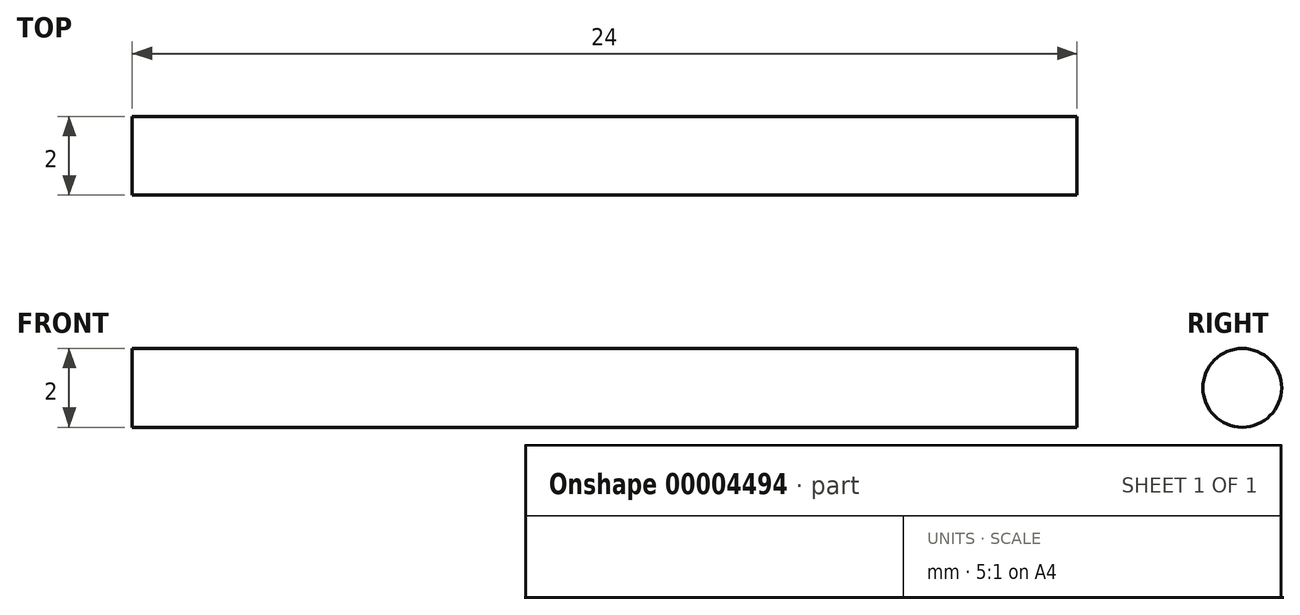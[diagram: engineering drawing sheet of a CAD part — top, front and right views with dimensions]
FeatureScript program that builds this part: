
annotation { "Feature Type Name" : "Feature", "Feature Type Description" : "" }
export const myFeature = defineFeature(function(context is Context, id is Id, definition is map)
    precondition{}
    {
        {
            var Q0;
            Q0=qCreatedBy(makeId("Right.planeOp"),FACE);
            var sketch = newSketch(context, id + "F0", { "sketchPlane" : qUnion([Q0])});
            skCircle(sketch, "E0", {"center": v(0, 0) * mm, "radius": 1 * mm});
            skSolve(sketch);
        }
        {
            var Q0;
            Q0=makeQuery(id+"F0.imprint","IMPRINT",FACE,{"disambiguationData":[TD([[makeQuery(id+"F0.imprint","IMPRINT",EDGE,{"derivedFrom":sQuery(id+"F0.wireOp",EDGE,"E0")}),1.0]])]});
            extrude(context, id + "F1", {"entities" : qUnion([Q0]), "endBound" : BoundingType.SYMMETRIC, "depth" : (20 + 4) * mm});
        }
    });
